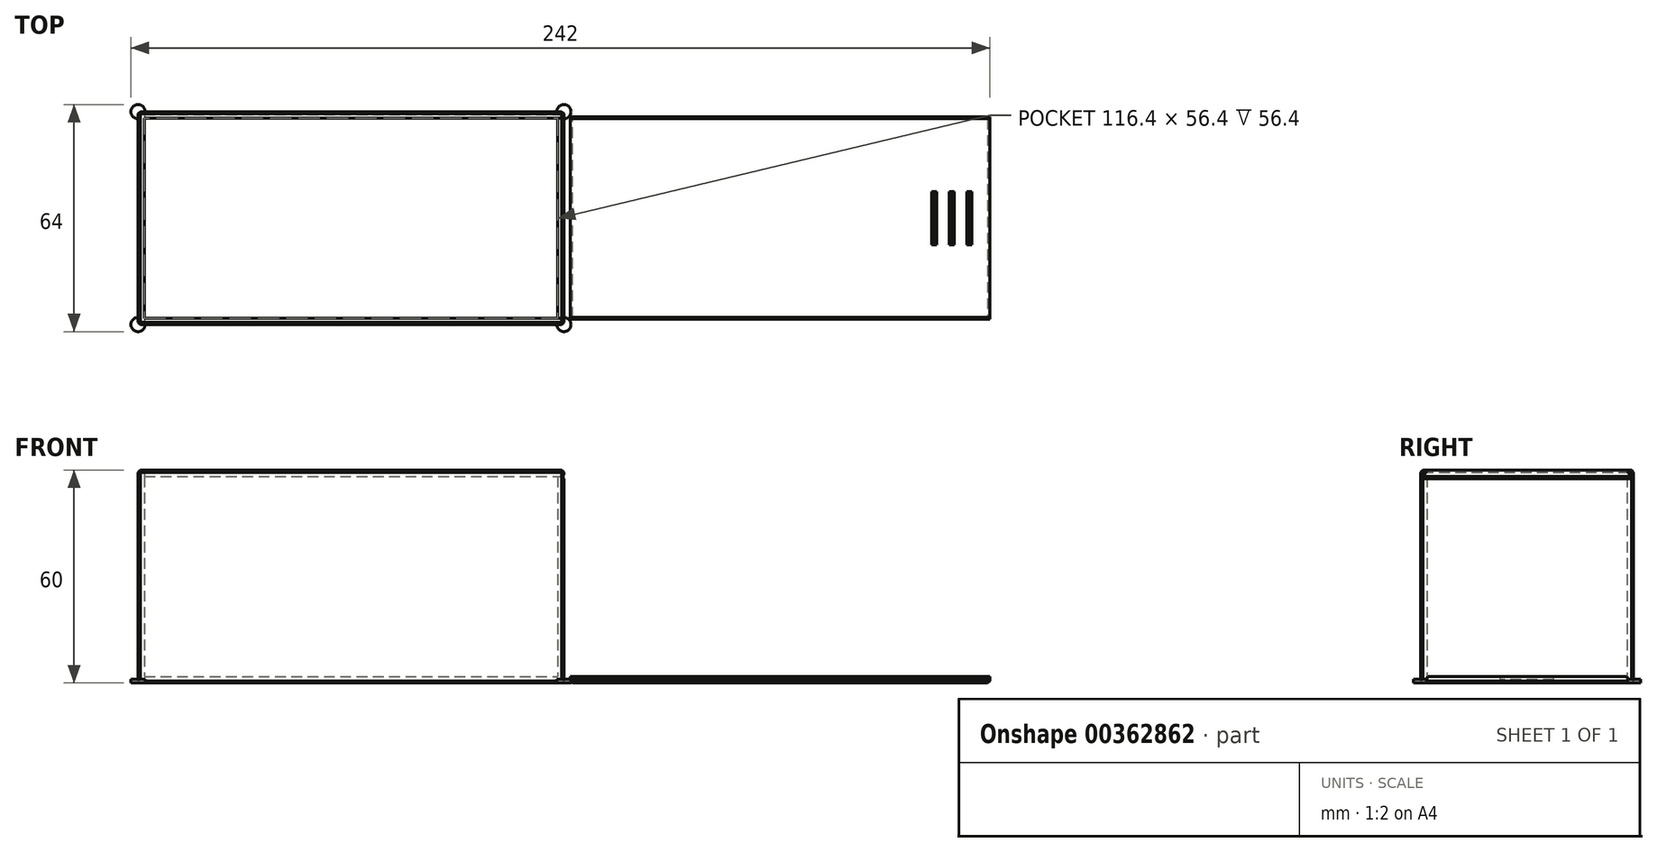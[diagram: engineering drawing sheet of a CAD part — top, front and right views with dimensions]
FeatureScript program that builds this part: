
annotation { "Feature Type Name" : "Feature", "Feature Type Description" : "" }
export const myFeature = defineFeature(function(context is Context, id is Id, definition is map)
    precondition{}
    {
        {
            assignVariable(context, id + "F0", {"name" : "Height", "anyValue" : 60});
        }
        {
            assignVariable(context, id + "F1", {"name" : "Length", "anyValue" : 120});
        }
        {
            assignVariable(context, id + "F2", {"name" : "WallThickness", "anyValue" : 1.8});
        }
        {
            var Q0;
            Q0=qCreatedBy(makeId("Top.planeOp"),FACE);
            var sketch = newSketch(context, id + "F3", { "sketchPlane" : qUnion([Q0])});
            skLineSegment(sketch, "E0", {"start": v(0, 0) * mm, "end": v(120, 0) * mm});
            skLineSegment(sketch, "E1", {"start": v(120, 0) * mm, "end": v(120, 60) * mm});
            skLineSegment(sketch, "E2", {"start": v(120, 60) * mm, "end": v(0, 60) * mm});
            skLineSegment(sketch, "E3", {"start": v(0, 60) * mm, "end": v(0, 0) * mm});
            skLineSegment(sketch, "E4.0", {"start": v(1.8, 1.8) * mm, "end": v(118.2, 1.8) * mm});
            skLineSegment(sketch, "E4.1", {"start": v(1.8, 58.2) * mm, "end": v(1.8, 1.8) * mm});
            skLineSegment(sketch, "E4.2", {"start": v(118.2, 58.2) * mm, "end": v(1.8, 58.2) * mm});
            skLineSegment(sketch, "E4.3", {"start": v(118.2, 1.8) * mm, "end": v(118.2, 58.2) * mm});
            skLineSegment(sketch, "E5", {"start": v(118.2, 1.8) * mm, "end": v(120, 1.8) * mm});
            skLineSegment(sketch, "E6", {"start": v(118.2, 58.2) * mm, "end": v(120, 58.2) * mm});
            skLineSegment(sketch, "E7", {"start": v(60, 60) * mm, "end": v(60, 0) * mm, "construction": true});
            skLineSegment(sketch, "E8", {"start": v(60.9, 1.8) * mm, "end": v(60.9, 58.2) * mm});
            skLineSegment(sketch, "E9.MirrorCS", {"start": v(59.1, 1.8) * mm, "end": v(59.1, 58.2) * mm});
            skSolve(sketch);
        }
        {
            var Q0;
            Q0=makeQuery(id+"F3.imprint","IMPRINT",FACE,{"disambiguationData":[TD([[makeQuery(id+"F3.imprint","IMPRINT",EDGE,{"derivedFrom":sQuery(id+"F3.wireOp",EDGE,"E0")}),1.0]])]});
            extrude(context, id + "F4", {"entities" : qUnion([Q0]), "depth" : (getVariable(context, 'Height')) * mm});
        }
        {
            var Q0;
            Q0=makeQuery(id+"F3.imprint","IMPRINT",FACE,{"disambiguationData":[TD([[makeQuery(id+"F3.imprint","IMPRINT",EDGE,{"derivedFrom":sQuery(id+"F3.wireOp",EDGE,"E4.0")}),1.0]])]});
            extrude(context, id + "F5", {"entities" : qUnion([Q0]), "operationType" : NewBodyOperationType.ADD, "depth" : (getVariable(context, 'WallThickness')) * mm});
        }
        {
            var Q0;
            Q0=makeQuery(id+"F3.imprint","IMPRINT",FACE,{"disambiguationData":[TD([[makeQuery(id+"F3.imprint","IMPRINT",EDGE,{"derivedFrom":sQuery(id+"F3.wireOp",EDGE,"E4.3")}),-1.0]])]});
            extrude(context, id + "F6", {"entities" : qUnion([Q0]), "operationType" : NewBodyOperationType.ADD, "depth" : (getVariable(context, 'Height') - getVariable(context, 'WallThickness')) * mm});
        }
        {
            var Q0;
            {var subQ0=sQuery(id+"F3.wireOp",EDGE,"E1");Q0=makeQuery(id+"F6.boolean.opBoolean","MERGE",FACE,{"derivedFrom":[makeQuery(id+"F4.opExtrude","SWEPT_FACE",FACE,{"disambiguationData":[OSD([subQ0]),TDD([makeQuery(id+"F3.imprint","IMPRINT",EDGE,{"disambiguationData":[TD([[makeQuery(id+"F3.imprint","INTERSECT",VERTEX,{"derivedFrom":[sQuery(id+"F3.wireOp",EDGE,"E0"),subQ0]}),-1.0]])],"derivedFrom":subQ0})])]}),makeQuery(id+"F4.opExtrude","SWEPT_FACE",FACE,{"disambiguationData":[OSD([subQ0]),TDD([makeQuery(id+"F3.imprint","IMPRINT",EDGE,{"disambiguationData":[TD([[makeQuery(id+"F3.imprint","INTERSECT",VERTEX,{"derivedFrom":[subQ0,sQuery(id+"F3.wireOp",EDGE,"E2")]}),1.0]])],"derivedFrom":subQ0})])]}),makeQuery(id+"F6.opExtrude","SWEPT_FACE",FACE,{"disambiguationData":[OSD([subQ0])]})]});}
            var sketch = newSketch(context, id + "F7", { "sketchPlane" : qUnion([Q0])});
            skLineSegment(sketch, "E10.0", {"start": v(1.8, 58.2) * mm, "end": v(58.2, 58.2) * mm});
            skLineSegment(sketch, "E10.1", {"start": v(0, 60) * mm, "end": v(1.8, 60) * mm, "construction": true});
            skLineSegment(sketch, "E10.2", {"start": v(58.2, 60) * mm, "end": v(60, 60) * mm, "construction": true});
            skLineSegment(sketch, "E10.3", {"start": v(60, 60) * mm, "end": v(60, 0) * mm, "construction": true});
            skLineSegment(sketch, "E10.4", {"start": v(0, 60) * mm, "end": v(0, 0) * mm, "construction": true});
            skLineSegment(sketch, "E11", {"start": v(1.8, 60) * mm, "end": v(0.76, 58.2) * mm});
            skLineSegment(sketch, "E12", {"start": v(0.76, 58.2) * mm, "end": v(1.8, 58.2) * mm});
            skPoint(sketch, "E13", {"position": v(30, 58.2) * mm});
            skLineSegment(sketch, "E14", {"start": v(30, 104.43) * mm, "end": v(30, 92.5) * mm, "construction": true});
            skLineSegment(sketch, "E15.MirrorCS", {"start": v(58.2, 60) * mm, "end": v(59.24, 58.2) * mm});
            skLineSegment(sketch, "E16.MirrorCS", {"start": v(59.24, 58.2) * mm, "end": v(58.2, 58.2) * mm});
            skLineSegment(sketch, "E17", {"start": v(1.8, 60) * mm, "end": v(58.2, 60) * mm});
            skLineSegment(sketch, "E18", {"start": v(0.96, 58.2) * mm, "end": v(2, 60) * mm});
            skLineSegment(sketch, "E19.MirrorCS", {"start": v(59.04, 58.2) * mm, "end": v(58, 60) * mm});
            skSolve(sketch);
        }
        {
            var Q0;
            Q0=makeQuery(id+"F7.imprint","IMPRINT",FACE,{"disambiguationData":[TD([[makeQuery(id+"F7.imprint","IMPRINT",EDGE,{"derivedFrom":sQuery(id+"F7.wireOp",EDGE,"E11")}),1.0]])]});
            var Q1;
            Q1=makeQuery(id+"F7.imprint","IMPRINT",FACE,{"disambiguationData":[TD([[makeQuery(id+"F7.imprint","IMPRINT",EDGE,{"derivedFrom":sQuery(id+"F7.wireOp",EDGE,"E15.MirrorCS")}),-1.0]])]});
            var Q2;
            {var subQ0=sQuery(id+"F7.wireOp",EDGE,"E12");var subQ3=sQuery(id+"F7.wireOp",EDGE,"E18");var subQ4=makeQuery(id+"F7.imprint","INTERSECT",VERTEX,{"derivedFrom":[subQ0,subQ3]});Q2=makeQuery(id+"F7.imprint","IMPRINT",FACE,{"disambiguationData":[TD([[makeQuery(id+"F7.imprint","IMPRINT",EDGE,{"disambiguationData":[TD([[subQ4,-1.0]])],"derivedFrom":subQ3}),-1.0]])]});}
            var Q3;
            {var subQ0=sQuery(id+"F7.wireOp",EDGE,"E16.MirrorCS");var subQ3=sQuery(id+"F7.wireOp",EDGE,"E19.MirrorCS");var subQ4=makeQuery(id+"F7.imprint","INTERSECT",VERTEX,{"derivedFrom":[subQ0,subQ3]});Q3=makeQuery(id+"F7.imprint","IMPRINT",FACE,{"disambiguationData":[TD([[makeQuery(id+"F7.imprint","IMPRINT",EDGE,{"disambiguationData":[TD([[subQ4,-1.0]])],"derivedFrom":subQ3}),1.0]])]});}
            extrude(context, id + "F8", {"entities" : qUnion([Q0, Q1, Q2, Q3]), "operationType" : NewBodyOperationType.REMOVE, "oppositeDirection" : true, "depth" : (getVariable(context, 'Length') - getVariable(context, 'WallThickness')) * mm});
        }
        {
            var Q0;
            Q0=makeQuery(id+"F7.imprint","IMPRINT",FACE,{"disambiguationData":[TD([[makeQuery(id+"F7.imprint","IMPRINT",EDGE,{"derivedFrom":sQuery(id+"F7.wireOp",EDGE,"E10.0")}),1.0]])]});
            var Q1;
            {var subQ0=sQuery(id+"F7.wireOp",EDGE,"E12");var subQ3=sQuery(id+"F7.wireOp",EDGE,"E18");var subQ4=makeQuery(id+"F7.imprint","INTERSECT",VERTEX,{"derivedFrom":[subQ0,subQ3]});Q1=makeQuery(id+"F7.imprint","IMPRINT",FACE,{"disambiguationData":[TD([[makeQuery(id+"F7.imprint","IMPRINT",EDGE,{"disambiguationData":[TD([[subQ4,-1.0]])],"derivedFrom":subQ3}),-1.0]])]});}
            var Q2;
            {var subQ0=sQuery(id+"F7.wireOp",EDGE,"E16.MirrorCS");var subQ3=sQuery(id+"F7.wireOp",EDGE,"E19.MirrorCS");var subQ4=makeQuery(id+"F7.imprint","INTERSECT",VERTEX,{"derivedFrom":[subQ0,subQ3]});Q2=makeQuery(id+"F7.imprint","IMPRINT",FACE,{"disambiguationData":[TD([[makeQuery(id+"F7.imprint","IMPRINT",EDGE,{"disambiguationData":[TD([[subQ4,-1.0]])],"derivedFrom":subQ3}),1.0]])]});}
            extrude(context, id + "F9", {"entities" : qUnion([Q0, Q1, Q2]), "depth" : (getVariable(context, 'Length')) * mm, "hasSecondDirection" : true, "secondDirectionOppositeDirection" : false, "secondDirectionDepth" : (getVariable(context, 'WallThickness')) * mm});
        }
        {
            var Q0;
            Q0=makeQuery(id+"F9.opExtrude","SWEPT_BODY",BODY,{"disambiguationData":[OSD([sQuery(id+"F7.wireOp",EDGE,"E10.0"),sQuery(id+"F7.wireOp",EDGE,"E12"),sQuery(id+"F7.wireOp",EDGE,"E16.MirrorCS"),sQuery(id+"F7.wireOp",EDGE,"E17"),sQuery(id+"F7.wireOp",EDGE,"E18"),sQuery(id+"F7.wireOp",EDGE,"E19.MirrorCS")])]});
            transform(context, id + "F10", {"entities" : qUnion([Q0]), "transformType" : TransformType.TRANSLATION_3D, "dx" : 0 * mm, "dy" : 0 * mm, "dz" : (-getVariable(context, 'Height') + getVariable(context, 'WallThickness')) * mm, "makeCopy" : false});
        }
        {
            var Q0;
            Q0=makeQuery(id+"F9.opExtrude","SWEPT_FACE",FACE,{"disambiguationData":[OSD([sQuery(id+"F7.wireOp",EDGE,"E17")])]});
            var sketch = newSketch(context, id + "F11", { "sketchPlane" : qUnion([Q0])});
            skLineSegment(sketch, "E20.0", {"start": v(240, 2) * mm, "end": v(240, 58) * mm, "construction": true});
            skLineSegment(sketch, "E20.1", {"start": v(240, 58) * mm, "end": v(121.8, 58) * mm, "construction": true});
            skLineSegment(sketch, "E20.2", {"start": v(240, 2) * mm, "end": v(121.8, 2) * mm, "construction": true});
            skLineSegment(sketch, "E20.3", {"start": v(121.8, 2) * mm, "end": v(121.8, 58) * mm, "construction": true});
            skLineSegment(sketch, "E21", {"start": v(235, 37.5) * mm, "end": v(235, 22.5) * mm});
            skLineSegment(sketch, "E22", {"start": v(235, 22.5) * mm, "end": v(232, 22.5) * mm});
            skLineSegment(sketch, "E23", {"start": v(232, 22.5) * mm, "end": v(232, 37.5) * mm});
            skLineSegment(sketch, "E24", {"start": v(232, 37.5) * mm, "end": v(235, 37.5) * mm});
            skPoint(sketch, "E25", {"position": v(235, 30) * mm});
            skPoint(sketch, "E26", {"position": v(240, 30) * mm});
            skLineSegment(sketch, "E27.1.0.0", {"start": v(230, 37.5) * mm, "end": v(230, 22.5) * mm});
            skLineSegment(sketch, "E27.1.0.1", {"start": v(230, 22.5) * mm, "end": v(227, 22.5) * mm});
            skLineSegment(sketch, "E27.1.0.2", {"start": v(227, 22.5) * mm, "end": v(227, 37.5) * mm});
            skLineSegment(sketch, "E27.1.0.3", {"start": v(227, 37.5) * mm, "end": v(230, 37.5) * mm});
            skLineSegment(sketch, "E27.2.0.0", {"start": v(225, 37.5) * mm, "end": v(225, 22.5) * mm});
            skLineSegment(sketch, "E27.2.0.1", {"start": v(225, 22.5) * mm, "end": v(222, 22.5) * mm});
            skLineSegment(sketch, "E27.2.0.2", {"start": v(222, 22.5) * mm, "end": v(222, 37.5) * mm});
            skLineSegment(sketch, "E27.2.0.3", {"start": v(222, 37.5) * mm, "end": v(225, 37.5) * mm});
            skLineSegment(sketch, "E27.direction1", {"start": v(232, 22.5) * mm, "end": v(227, 22.5) * mm, "construction": true});
            skSolve(sketch);
        }
        {
            var Q0;
            Q0=makeQuery(id+"F11.imprint","IMPRINT",FACE,{"disambiguationData":[TD([[makeQuery(id+"F11.imprint","IMPRINT",EDGE,{"derivedFrom":sQuery(id+"F11.wireOp",EDGE,"E27.2.0.0")}),-1.0]])]});
            var Q1;
            Q1=makeQuery(id+"F11.imprint","IMPRINT",FACE,{"disambiguationData":[TD([[makeQuery(id+"F11.imprint","IMPRINT",EDGE,{"derivedFrom":sQuery(id+"F11.wireOp",EDGE,"E27.1.0.0")}),-1.0]])]});
            var Q2;
            Q2=makeQuery(id+"F11.imprint","IMPRINT",FACE,{"disambiguationData":[TD([[makeQuery(id+"F11.imprint","IMPRINT",EDGE,{"derivedFrom":sQuery(id+"F11.wireOp",EDGE,"E21")}),-1.0]])]});
            extrude(context, id + "F12", {"entities" : qUnion([Q0, Q1, Q2]), "operationType" : NewBodyOperationType.REMOVE, "oppositeDirection" : true, "depth" : (getVariable(context, 'WallThickness') / 2) * mm});
        }
        {
            var Q0;
            Q0=makeQuery(id+"F12.boolean.opBoolean","COPY",EDGE,{"derivedFrom":makeQuery(id+"F12.opExtrude","CAP_EDGE",EDGE,{"disambiguationData":[OSD([sQuery(id+"F11.wireOp",EDGE,"E23")])],"isStart":false})});
            var Q1;
            Q1=makeQuery(id+"F12.boolean.opBoolean","COPY",EDGE,{"derivedFrom":makeQuery(id+"F12.opExtrude","CAP_EDGE",EDGE,{"disambiguationData":[OSD([sQuery(id+"F11.wireOp",EDGE,"E27.1.0.2")])],"isStart":false})});
            var Q2;
            Q2=makeQuery(id+"F12.boolean.opBoolean","COPY",EDGE,{"derivedFrom":makeQuery(id+"F12.opExtrude","CAP_EDGE",EDGE,{"disambiguationData":[OSD([sQuery(id+"F11.wireOp",EDGE,"E27.2.0.2")])],"isStart":false})});
            chamfer(context, id + "F13", {"entities" : qUnion([Q0, Q1, Q2]), "width" : 2.5 * mm, "tangentPropagation" : true});
        }
        {
            var Q0;
            Q0=makeQuery(id+"F4.opExtrude","SWEPT_FACE",FACE,{"disambiguationData":[OSD([sQuery(id+"F3.wireOp",EDGE,"E0")])]});
            var sketch = newSketch(context, id + "F14", { "sketchPlane" : qUnion([Q0])});
            skLineSegment(sketch, "E28.0", {"start": v(0, 60) * mm, "end": v(0, 0) * mm, "construction": true});
            skLineSegment(sketch, "E28.1", {"start": v(0, 60) * mm, "end": v(120, 60) * mm, "construction": true});
            skLineSegment(sketch, "E28.2", {"start": v(120, 60) * mm, "end": v(120, 0) * mm, "construction": true});
            skLineSegment(sketch, "E28.3", {"start": v(0, 0) * mm, "end": v(120, 0) * mm, "construction": true});
            skLineSegment(sketch, "E29", {"start": v(0, 30) * mm, "end": v(120, 30) * mm, "construction": true});
            skLineSegment(sketch, "E30", {"start": v(60, 60) * mm, "end": v(60, 0) * mm, "construction": true});
            skLineSegment(sketch, "E31", {"start": v(60, 48) * mm, "end": v(54, 48) * mm});
            skLineSegment(sketch, "E32", {"start": v(54, 48) * mm, "end": v(54, 36) * mm});
            skLineSegment(sketch, "E33", {"start": v(54, 36) * mm, "end": v(42, 36) * mm});
            skLineSegment(sketch, "E34", {"start": v(42, 36) * mm, "end": v(42, 30) * mm});
            skLineSegment(sketch, "E35.MirrorCS", {"start": v(60, 48) * mm, "end": v(66, 48) * mm});
            skLineSegment(sketch, "E36.MirrorCS", {"start": v(66, 48) * mm, "end": v(66, 36) * mm});
            skLineSegment(sketch, "E37.MirrorCS", {"start": v(78, 36) * mm, "end": v(78, 30) * mm});
            skLineSegment(sketch, "E38.MirrorCS", {"start": v(66, 36) * mm, "end": v(78, 36) * mm});
            skLineSegment(sketch, "E39.MirrorCS", {"start": v(42, 24) * mm, "end": v(42, 30) * mm});
            skLineSegment(sketch, "E40.MirrorCS", {"start": v(54, 24) * mm, "end": v(42, 24) * mm});
            skLineSegment(sketch, "E41.MirrorCS", {"start": v(54, 12) * mm, "end": v(54, 24) * mm});
            skLineSegment(sketch, "E42.MirrorCS", {"start": v(60, 12) * mm, "end": v(54, 12) * mm});
            skLineSegment(sketch, "E43.MirrorCS", {"start": v(60, 12) * mm, "end": v(66, 12) * mm});
            skLineSegment(sketch, "E44.MirrorCS", {"start": v(66, 12) * mm, "end": v(66, 24) * mm});
            skLineSegment(sketch, "E45.MirrorCS", {"start": v(78, 24) * mm, "end": v(78, 30) * mm});
            skLineSegment(sketch, "E46.MirrorCS", {"start": v(66, 24) * mm, "end": v(78, 24) * mm});
            skSolve(sketch);
        }
        {
            var Q0;
            Q0=makeQuery(id+"F4.opExtrude","SWEPT_FACE",FACE,{"disambiguationData":[OSD([sQuery(id+"F3.wireOp",EDGE,"E0")])]});
            var Q1;
            {var subQ0=sQuery(id+"F3.wireOp",EDGE,"E1");Q1=makeQuery(id+"F6.boolean.opBoolean","MERGE",FACE,{"derivedFrom":[makeQuery(id+"F4.opExtrude","SWEPT_FACE",FACE,{"disambiguationData":[OSD([subQ0]),TDD([makeQuery(id+"F3.imprint","IMPRINT",EDGE,{"disambiguationData":[TD([[makeQuery(id+"F3.imprint","INTERSECT",VERTEX,{"derivedFrom":[sQuery(id+"F3.wireOp",EDGE,"E0"),subQ0]}),-1.0]])],"derivedFrom":subQ0})])]}),makeQuery(id+"F4.opExtrude","SWEPT_FACE",FACE,{"disambiguationData":[OSD([subQ0]),TDD([makeQuery(id+"F3.imprint","IMPRINT",EDGE,{"disambiguationData":[TD([[makeQuery(id+"F3.imprint","INTERSECT",VERTEX,{"derivedFrom":[subQ0,sQuery(id+"F3.wireOp",EDGE,"E2")]}),1.0]])],"derivedFrom":subQ0})])]}),makeQuery(id+"F6.opExtrude","SWEPT_FACE",FACE,{"disambiguationData":[OSD([subQ0])]})]});}
            var Q2;
            Q2=makeQuery(id+"F4.opExtrude","SWEPT_FACE",FACE,{"disambiguationData":[OSD([sQuery(id+"F3.wireOp",EDGE,"E2")])]});
            var Q3;
            Q3=makeQuery(id+"F4.opExtrude","SWEPT_FACE",FACE,{"disambiguationData":[OSD([sQuery(id+"F3.wireOp",EDGE,"E3")])]});
            var Q4;
            {var subQ0=sQuery(id+"F3.wireOp",EDGE,"E6");var subQ1=sQuery(id+"F3.wireOp",EDGE,"E5");var subQ2=sQuery(id+"F3.wireOp",EDGE,"E4.3");var subQ3=sQuery(id+"F3.wireOp",EDGE,"E1");var subQ4=sQuery(id+"F3.wireOp",EDGE,"E4.2");var subQ5=sQuery(id+"F3.wireOp",EDGE,"E4.1");var subQ6=sQuery(id+"F3.wireOp",EDGE,"E4.0");Q4=makeQuery(id+"F6.boolean.opBoolean","MERGE",FACE,{"derivedFrom":[makeQuery(id+"F5.boolean.opBoolean","MERGE",FACE,{"derivedFrom":[makeQuery(id+"F4.opExtrude","CAP_FACE",FACE,{"disambiguationData":[OSD([sQuery(id+"F3.wireOp",EDGE,"E0"),subQ3,sQuery(id+"F3.wireOp",EDGE,"E2"),sQuery(id+"F3.wireOp",EDGE,"E3"),subQ6,subQ5,subQ4,subQ1,subQ0])],"isStart":true}),makeQuery(id+"F5.opExtrude","CAP_FACE",FACE,{"disambiguationData":[OSD([subQ6,subQ5,subQ4,subQ2])],"isStart":true})]}),makeQuery(id+"F6.opExtrude","CAP_FACE",FACE,{"disambiguationData":[OSD([subQ3,subQ2,subQ1,subQ0])],"isStart":true})]});}
            var Q5;
            Q5=makeQuery(id+"F9.opExtrude","SWEPT_FACE",FACE,{"disambiguationData":[OSD([sQuery(id+"F7.wireOp",EDGE,"E10.0"),sQuery(id+"F7.wireOp",EDGE,"E12"),sQuery(id+"F7.wireOp",EDGE,"E16.MirrorCS")])]});
            chamfer(context, id + "F15", {"entities" : qUnion([Q0, Q1, Q2, Q3, Q4, Q5]), "width" : 0.6 * mm, "tangentPropagation" : true});
        }
        {
            var Q0;
            Q0=qCreatedBy(makeId("Top.planeOp"),FACE);
            var sketch = newSketch(context, id + "F16", { "sketchPlane" : qUnion([Q0])});
            skCircle(sketch, "E47", {"center": v(0, 60) * mm, "radius": 2 * mm});
            skCircle(sketch, "E48", {"center": v(120, 60) * mm, "radius": 2 * mm});
            skCircle(sketch, "E49", {"center": v(120, 0) * mm, "radius": 2 * mm});
            skCircle(sketch, "E50", {"center": v(0, 0) * mm, "radius": 2 * mm});
            skSolve(sketch);
        }
        {
            var Q0;
            Q0 = qSketchRegion(id + "F16", true);
            extrude(context, id + "F17", {"entities" : qUnion([Q0]), "operationType" : NewBodyOperationType.ADD, "depth" : 1 * mm});
        }
    });
